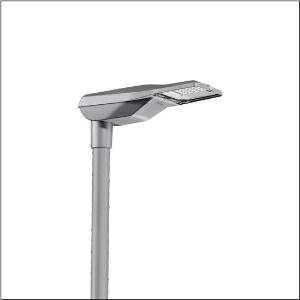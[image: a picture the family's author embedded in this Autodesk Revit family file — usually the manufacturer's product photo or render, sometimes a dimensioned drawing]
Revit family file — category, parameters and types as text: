
# Revit family: streetlight_sl_21_iq_micro___st1_0a_5xe1d31d08cb_abfe
name_source: partatom
category: Lighting Fixtures
units: mm (PartAtom-declared; Revit-internal decimal feet)

## family parameters
Cut with Voids When Loaded = No
Host = Face
Light Source = No
Part Type = Normal
Room Calculation Point = No
Round Connector Dimension = Use Diameter
Shared = No

## types (1)
- --- (1 x LED, 2870 lm, 19.4 W, 3000K)
    Apparent Load = 19 VA
    CIE Flux Codes = 37 72 97 100 100
    Color Rendering = 70
    Color Temperature = 3000K
    Default Elevation = 1800 mm
    Description = Streetlight SL 21 iQ micro, mast luminaire, primary light control with lens, of PMMA, primary optical cover: cover, of toughened safety glass, transparent, light distribution: ST1.0a, light emission: direct distribution, primary light characteristic: asymmetric, installation type: post-top, side-entry, LED, High Power LED, rated luminous flux: 2.870lm, luminous efficacy: 148lm/W, light colour: 730, colour temperature: 3000K, control: Auto-Match, Temp-Guard, Lumen-Switch, Night-Set, Smart-Wire, Light-Fading, Desk-Remote (wireless, voltage-free reading and setting of iQ features in the workshop via application-optimized NFC function/RFID function), optimised constant luminous flux control (CLO 2.0), presetting dimming linear, mains connection: 220..240V, AC, 50/60Hz, start of lifetime: 19W, end of service life: 20W, reduction: 10W, luminaire housing, of diecast aluminium, powder-coated, Siteco® metallic grey (DB 702S), corrosivity category C5 mid according to DIN EN ISO 12944, please order mast flange separately, inclination adjustable: 0°, 5°, 10°, 15°, sealing non-destructively replaceable, multi-level sealing system, length: 528mm, width: 235mm, height: 110mm, mast flange for spigot size: 42mm (side-entry): 5XC10008XM4, 60/48mm (side-entry/post-top): 5XC10108XM2, 76/60mm (side-entry/post-top): 5XC10108XM1, protection rating (complete): IP66, insulation class (complete): insulation class II (safety insulation), certification: CE, ENEC, ENEC+, VDE, impact resistance: IK09, permissible operating ambient temperature for outdoor applications: -40..+50°C, standard-compliant lighting for roads and squares, packaging unit: 1 piece

Light Distribution: ST1.0a
    Height = 110 mm
    Lamp = 1 x LED
    Lamp Light Flux = 2870 lm
    Lamp Power = 19.4 W
    Lamp count = 1
    Length = 528 mm
    Luminous efficacy = 148 lm/W
    Manufacturer = Siteco
    ModVariant = No
    Model = 5XE1D31D08CB
    Number of Poles = 1
    OnlyDefault = Yes
    Power Factor = 1
    Product Name = Streetlight SL 21 iQ micro | ST1.0a
    Product group = mast luminaire | pylon top
    ProductGroupID = 6100
    Protection Class = Protection class II
    Protection Degree = IP 66
    RLX_Detail_Level = 1
    RLX_Emergency_Light_Flux = 0 lm
    RLX_Emergency_Type = 0
    RLX_Emergency_Type_DB = No
    RlxData = <blob elided: 98649 chars, md5=3b9ef94f>
    Socket = socket
    Standby Power = 0 W
    System Light Flux = 2870 lm
    System Power = 19 W
    Type Comments = factory setting: luminous flux: 100 % | dim-lin: 254 | 387 mA
    Type Image = l_1006881.jpg
    URL = http://relux.com
    VarID = @adj_070613
    Voltage = 0 V
    Weight = 0.00 kg
    Width = 235 mm

## geometry (parser evidence)
native form markers: Blend x4, Sweep x9
no freeform markers — native parametric forms only
